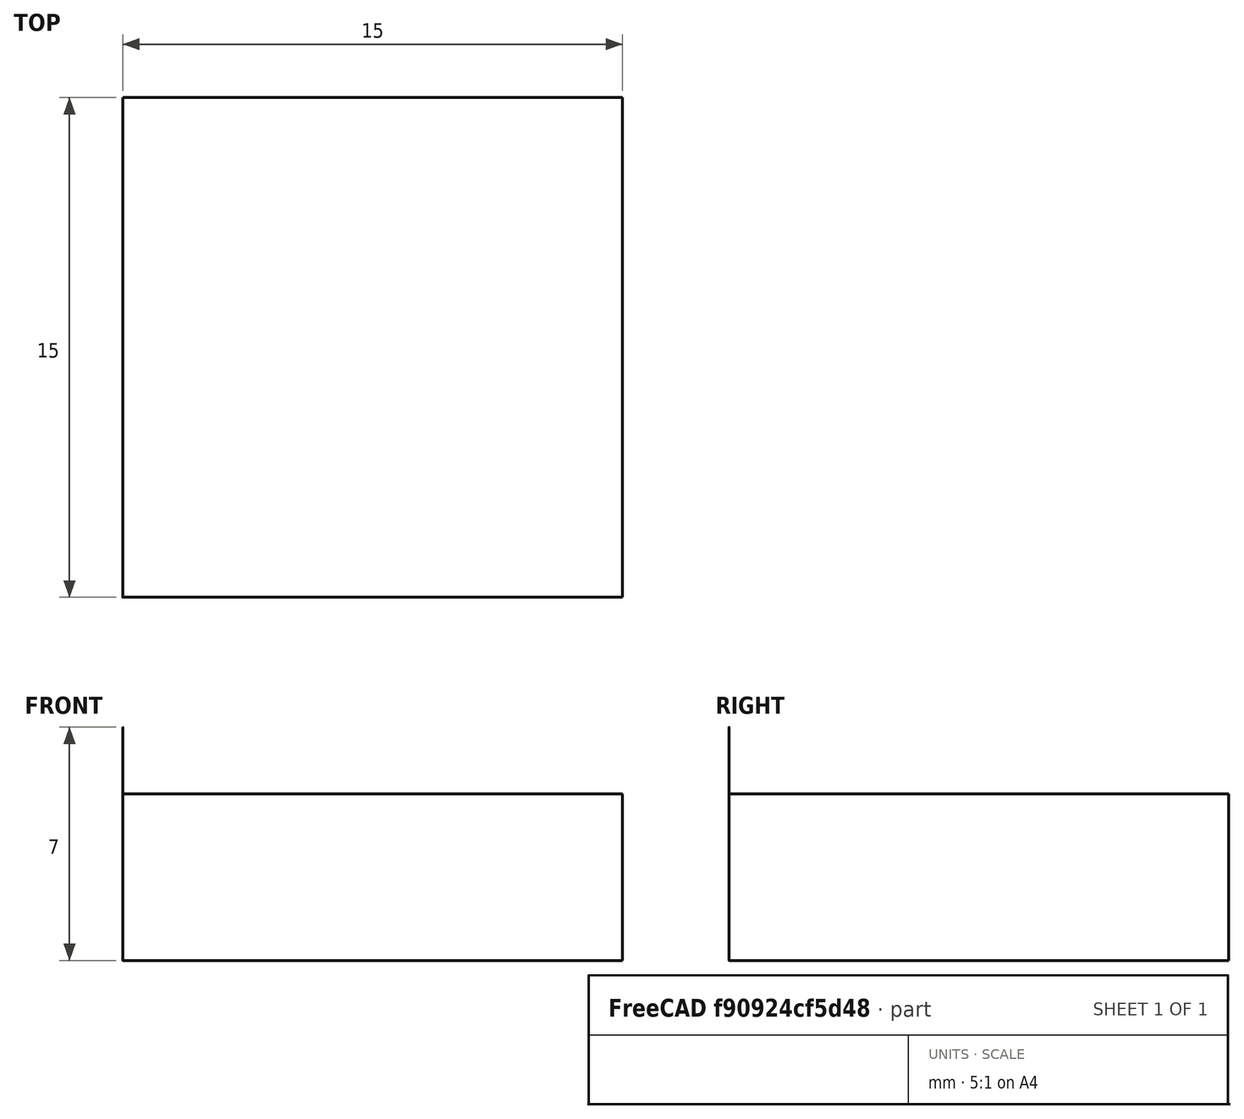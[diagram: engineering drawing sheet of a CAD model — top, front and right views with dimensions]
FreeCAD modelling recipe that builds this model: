
FCSTD DOCUMENT  (FreeCAD 1.0R39109 (Git))
Label: BoxWith25GridPockets
License: All rights reserved
LicenseURL: https://en.wikipedia.org/wiki/All_rights_reserved
objects: Part::Box×26, Part::Cut×25, Part::FeaturePython×4, App::DocumentObjectGroup×3, Path::FeaturePython×3, App::FeaturePython×1
note: 56 computed .brp shape members not serialized (recipe doc carries the construction recipe); baked Part::Feature solids carry a one-line shape summary decoded from their .brp

FEATURE [Part::Box] Box
  AttacherType = Attacher::AttachEngine3D
  Height = 5
  Length = 15
  Width = 15
FEATURE [Part::Box] Pocket_0_0
  AttacherType = Attacher::AttachEngine3D
  Height = 0.05
  Length = 0.2
  Placement = pos=(2.33333,2.33333,4.95) rot=(0,0,1;0rad)
  Width = 0.2
FEATURE [Part::Box] Pocket_0_1
  AttacherType = Attacher::AttachEngine3D
  Height = 0.05
  Length = 0.2
  Placement = pos=(4.86667,2.33333,4.95) rot=(0,0,1;0rad)
  Width = 0.2
FEATURE [Part::Box] Pocket_0_2
  AttacherType = Attacher::AttachEngine3D
  Height = 0.05
  Length = 0.2
  Placement = pos=(7.4,2.33333,4.95) rot=(0,0,1;0rad)
  Width = 0.2
FEATURE [Part::Box] Pocket_0_3
  AttacherType = Attacher::AttachEngine3D
  Height = 0.05
  Length = 0.2
  Placement = pos=(9.93333,2.33333,4.95) rot=(0,0,1;0rad)
  Width = 0.2
FEATURE [Part::Box] Pocket_0_4
  AttacherType = Attacher::AttachEngine3D
  Height = 0.05
  Length = 0.2
  Placement = pos=(12.4667,2.33333,4.95) rot=(0,0,1;0rad)
  Width = 0.2
FEATURE [Part::Box] Pocket_1_0
  AttacherType = Attacher::AttachEngine3D
  Height = 0.05
  Length = 0.2
  Placement = pos=(2.33333,4.86667,4.95) rot=(0,0,1;0rad)
  Width = 0.2
FEATURE [Part::Box] Pocket_1_1
  AttacherType = Attacher::AttachEngine3D
  Height = 0.05
  Length = 0.2
  Placement = pos=(4.86667,4.86667,4.95) rot=(0,0,1;0rad)
  Width = 0.2
FEATURE [Part::Box] Pocket_1_2
  AttacherType = Attacher::AttachEngine3D
  Height = 0.05
  Length = 0.2
  Placement = pos=(7.4,4.86667,4.95) rot=(0,0,1;0rad)
  Width = 0.2
FEATURE [Part::Box] Pocket_1_3
  AttacherType = Attacher::AttachEngine3D
  Height = 0.05
  Length = 0.2
  Placement = pos=(9.93333,4.86667,4.95) rot=(0,0,1;0rad)
  Width = 0.2
FEATURE [Part::Box] Pocket_1_4
  AttacherType = Attacher::AttachEngine3D
  Height = 0.05
  Length = 0.2
  Placement = pos=(12.4667,4.86667,4.95) rot=(0,0,1;0rad)
  Width = 0.2
FEATURE [Part::Box] Pocket_2_0
  AttacherType = Attacher::AttachEngine3D
  Height = 0.05
  Length = 0.2
  Placement = pos=(2.33333,7.4,4.95) rot=(0,0,1;0rad)
  Width = 0.2
FEATURE [Part::Box] Pocket_2_1
  AttacherType = Attacher::AttachEngine3D
  Height = 0.05
  Length = 0.2
  Placement = pos=(4.86667,7.4,4.95) rot=(0,0,1;0rad)
  Width = 0.2
FEATURE [Part::Box] Pocket_2_2
  AttacherType = Attacher::AttachEngine3D
  Height = 0.05
  Length = 0.2
  Placement = pos=(7.4,7.4,4.95) rot=(0,0,1;0rad)
  Width = 0.2
FEATURE [Part::Box] Pocket_2_3
  AttacherType = Attacher::AttachEngine3D
  Height = 0.05
  Length = 0.2
  Placement = pos=(9.93333,7.4,4.95) rot=(0,0,1;0rad)
  Width = 0.2
FEATURE [Part::Box] Pocket_2_4
  AttacherType = Attacher::AttachEngine3D
  Height = 0.05
  Length = 0.2
  Placement = pos=(12.4667,7.4,4.95) rot=(0,0,1;0rad)
  Width = 0.2
FEATURE [Part::Box] Pocket_3_0
  AttacherType = Attacher::AttachEngine3D
  Height = 0.05
  Length = 0.2
  Placement = pos=(2.33333,9.93333,4.95) rot=(0,0,1;0rad)
  Width = 0.2
FEATURE [Part::Box] Pocket_3_1
  AttacherType = Attacher::AttachEngine3D
  Height = 0.05
  Length = 0.2
  Placement = pos=(4.86667,9.93333,4.95) rot=(0,0,1;0rad)
  Width = 0.2
FEATURE [Part::Box] Pocket_3_2
  AttacherType = Attacher::AttachEngine3D
  Height = 0.05
  Length = 0.2
  Placement = pos=(7.4,9.93333,4.95) rot=(0,0,1;0rad)
  Width = 0.2
FEATURE [Part::Box] Pocket_3_3
  AttacherType = Attacher::AttachEngine3D
  Height = 0.05
  Length = 0.2
  Placement = pos=(9.93333,9.93333,4.95) rot=(0,0,1;0rad)
  Width = 0.2
FEATURE [Part::Box] Pocket_3_4
  AttacherType = Attacher::AttachEngine3D
  Height = 0.05
  Length = 0.2
  Placement = pos=(12.4667,9.93333,4.95) rot=(0,0,1;0rad)
  Width = 0.2
FEATURE [Part::Box] Pocket_4_0
  AttacherType = Attacher::AttachEngine3D
  Height = 0.05
  Length = 0.2
  Placement = pos=(2.33333,12.4667,4.95) rot=(0,0,1;0rad)
  Width = 0.2
FEATURE [Part::Box] Pocket_4_1
  AttacherType = Attacher::AttachEngine3D
  Height = 0.05
  Length = 0.2
  Placement = pos=(4.86667,12.4667,4.95) rot=(0,0,1;0rad)
  Width = 0.2
FEATURE [Part::Box] Pocket_4_2
  AttacherType = Attacher::AttachEngine3D
  Height = 0.05
  Length = 0.2
  Placement = pos=(7.4,12.4667,4.95) rot=(0,0,1;0rad)
  Width = 0.2
FEATURE [Part::Box] Pocket_4_3
  AttacherType = Attacher::AttachEngine3D
  Height = 0.05
  Length = 0.2
  Placement = pos=(9.93333,12.4667,4.95) rot=(0,0,1;0rad)
  Width = 0.2
FEATURE [Part::Box] Pocket_4_4
  AttacherType = Attacher::AttachEngine3D
  Height = 0.05
  Length = 0.2
  Placement = pos=(12.4667,12.4667,4.95) rot=(0,0,1;0rad)
  Width = 0.2
FEATURE [Part::Cut] Cut  label="Cut_0"
  Base = -> Box
  Refine = true
  Tool = -> Pocket_0_0
FEATURE [Part::Cut] Cut001  label="Cut_1"
  Base = -> Cut
  Refine = true
  Tool = -> Pocket_0_1
FEATURE [Part::Cut] Cut002  label="Cut_2"
  Base = -> Cut001
  Refine = true
  Tool = -> Pocket_0_2
FEATURE [Part::Cut] Cut003  label="Cut_3"
  Base = -> Cut002
  Refine = true
  Tool = -> Pocket_0_3
FEATURE [Part::Cut] Cut004  label="Cut_4"
  Base = -> Cut003
  Refine = true
  Tool = -> Pocket_0_4
FEATURE [Part::Cut] Cut005  label="Cut_5"
  Base = -> Cut004
  Refine = true
  Tool = -> Pocket_1_0
FEATURE [Part::Cut] Cut006  label="Cut_6"
  Base = -> Cut005
  Refine = true
  Tool = -> Pocket_1_1
FEATURE [Part::Cut] Cut007  label="Cut_7"
  Base = -> Cut006
  Refine = true
  Tool = -> Pocket_1_2
FEATURE [Part::Cut] Cut008  label="Cut_8"
  Base = -> Cut007
  Refine = true
  Tool = -> Pocket_1_3
FEATURE [Part::Cut] Cut009  label="Cut_9"
  Base = -> Cut008
  Refine = true
  Tool = -> Pocket_1_4
FEATURE [Part::Cut] Cut010  label="Cut_10"
  Base = -> Cut009
  Refine = true
  Tool = -> Pocket_2_0
FEATURE [Part::Cut] Cut011  label="Cut_11"
  Base = -> Cut010
  Refine = true
  Tool = -> Pocket_2_1
FEATURE [Part::Cut] Cut012  label="Cut_12"
  Base = -> Cut011
  Refine = true
  Tool = -> Pocket_2_2
FEATURE [Part::Cut] Cut013  label="Cut_13"
  Base = -> Cut012
  Refine = true
  Tool = -> Pocket_2_3
FEATURE [Part::Cut] Cut014  label="Cut_14"
  Base = -> Cut013
  Refine = true
  Tool = -> Pocket_2_4
FEATURE [Part::Cut] Cut015  label="Cut_15"
  Base = -> Cut014
  Refine = true
  Tool = -> Pocket_3_0
FEATURE [Part::Cut] Cut016  label="Cut_16"
  Base = -> Cut015
  Refine = true
  Tool = -> Pocket_3_1
FEATURE [Part::Cut] Cut017  label="Cut_17"
  Base = -> Cut016
  Refine = true
  Tool = -> Pocket_3_2
FEATURE [Part::Cut] Cut018  label="Cut_18"
  Base = -> Cut017
  Refine = true
  Tool = -> Pocket_3_3
FEATURE [Part::Cut] Cut019  label="Cut_19"
  Base = -> Cut018
  Refine = true
  Tool = -> Pocket_3_4
FEATURE [Part::Cut] Cut020  label="Cut_20"
  Base = -> Cut019
  Refine = true
  Tool = -> Pocket_4_0
FEATURE [Part::Cut] Cut021  label="Cut_21"
  Base = -> Cut020
  Refine = true
  Tool = -> Pocket_4_1
FEATURE [Part::Cut] Cut022  label="Cut_22"
  Base = -> Cut021
  Refine = true
  Tool = -> Pocket_4_2
FEATURE [Part::Cut] Cut023  label="Cut_23"
  Base = -> Cut022
  Refine = true
  Tool = -> Pocket_4_3
FEATURE [Part::Cut] Cut024  label="Cut_24"
  Base = -> Cut023
  Refine = true
  Tool = -> Pocket_4_4
FEATURE [App::FeaturePython] SetupSheet  # Path/CAM operation (typed FeaturePython)
  ClearanceHeightExpression = OpStockZMax+SetupSheet.ClearanceHeightOffset
  ClearanceHeightOffset = 5
  CoolantMode = 0
  CoolantModes = None | Flood | Mist
  FinalDepthExpression = OpFinalDepth
  HorizRapid = 333.333
  SafeHeightExpression = OpStockZMax+SetupSheet.SafeHeightOffset
  SafeHeightOffset = 3
  StartDepthExpression = OpStartDepth
  StepDownExpression = OpToolDiameter
  VertRapid = 0
FEATURE [Part::FeaturePython] Clone  label="Model-Cut_24"  # Draft clone (typed FeaturePython)
  AttacherType = Attacher::AttachEngine3D
  Fuse = false
  Objects = -> [Cut024]
  PathResource = Model
  Scale = (1,1,1)
FEATURE [App::DocumentObjectGroup] Model
  Group = -> [Clone]
FEATURE [Part::FeaturePython] ToolBit  label="Drill"  # Path/CAM toolbit (typed FeaturePython)
  BitPropertyNames = Chipload | Diameter | Flutes | Length | Material | TipAngle
  BitShape = <path>
  Chipload = 0
  Diameter = 0.005
  Flutes = 0
  Length = 7
  Material = 0
  ShapeName = drill
  TipAngle = 119
FEATURE [Part::FeaturePython] Stock  # WARN: FeaturePython — macro-defined, semantics opaque (R4)
  Base = -> Model
  ExtXneg = 0.001
  ExtXpos = 0.001
  ExtYneg = 0.001
  ExtYpos = 0.001
  ExtZneg = 0.001
  ExtZpos = 0.001
  StockType = FromBase
FEATURE [Part::FeaturePython] ToolBit001  label="Drill003"  # Path/CAM toolbit (typed FeaturePython)
  BitPropertyNames = Chipload | Diameter | Flutes | Length | Material | TipAngle
  BitShape = <path>
  Chipload = 0
  Diameter = 0.005
  Flutes = 0
  Length = 7
  Material = 0
  ShapeName = drill
  TipAngle = 119
FEATURE [Path::FeaturePython] TC__Default_Tool  label="TC: Default Tool"  # Path/CAM operation (typed FeaturePython)
  HorizFeed = 0
  HorizRapid = 333.333
  SpindleDir = 0
  SpindleSpeed = 0
  Tool = -> ToolBit001
  ToolNumber = 1
  VertFeed = 0
  VertRapid = 0
  expr: HorizRapid = SetupSheet.HorizRapid
  expr: VertRapid = SetupSheet.VertRapid
FEATURE [App::DocumentObjectGroup] Tools
  Group = -> [TC__Default_Tool]
FEATURE [Path::FeaturePython] Pocket_Shape  # Path/CAM operation (typed FeaturePython)
  Active = true
  AreaParams:
    Tolerance = 1e-07
    FitArcs = True
    Simplify = False
    CleanDistance = 0.0
    Accuracy = 0.01
    Unit = 1.0
    MinArcPoints = 4
    MaxArcPoints = 100
    ClipperScale = 10000000.0
    Fill = 0
    Coplanar = 0
    Reorient = True
    Outline = False
    Explode = False
    OpenMode = 0
    Deflection = 0.01
    SubjectFill = 0
    ClipFill = 0
    Offset = 0.0
    ExtraPass = 0
    Stepover = 0.0
    LastStepover = 0.0
    JoinType = 0
    EndType = 0
    MiterLimit = 2.0
    RoundPrecision = 0.0
    PocketMode = 1
    ToolRadius = 0.0025
    PocketExtraOffset = 0.0
    PocketStepover = 0.0025
    PocketLastStepover = 0.0
    FromCenter = True
    Angle = 0.0
    AngleShift = 0.0
    Shift = 0.0
    Thicken = False
    SectionCount = -1
    Stepdown = 1.0
    SectionOffset = 0.0
    SectionTolerance = 1e-06
    SectionMode = 2
    Project = False
  Base = -> [Clone]
  ClearanceHeight = 10.001
  CoolantMode = 0
  CutMode = 0
  CycleTime = Cycletime Error
  ExtensionCorners = true
  ExtensionLengthDefault = 0.0025
  ExtraOffset = 0
  FinalDepth = 4.95
  FinishDepth = 0
  KeepToolDown = false
  MinTravel = false
  OffsetPattern = 0
  OpFinalDepth = 4.95
  OpStartDepth = 5.001
  OpStockZMax = 5.001
  OpStockZMin = -0.001
  OpToolDiameter = 0.005
  PathParams = {'orientation': 1, 'feedrate': 0.0, 'feedrate_v': 0.0, 'verbose': True, 'resume_height': 8.001000000000001, 'retraction': 10.001000000000001, 'return_end': True, 'preamble': False, 'start': Vector (12.664166566666669, 10.130833333333333, 10.001000000000001)}
  PocketLastStepOver = 0
  SafeHeight = 8.001
  SplitArcs = false
  StartAt = 0
  StartDepth = 5.001
  StartPoint = (0,0,0)
  StepDown = 0.005
  StepOver = 50
  ToolController = -> TC__Default_Tool
  UseOutline = false
  UseRestMachining = false
  UseStartPoint = false
  ZigZagAngle = 0
  expr: ClearanceHeight = OpStockZMax + SetupSheet.ClearanceHeightOffset
  expr: ExtensionLengthDefault = OpToolDiameter / 2
  expr: FinalDepth = OpFinalDepth
  expr: SafeHeight = OpStockZMax + SetupSheet.SafeHeightOffset
  expr: StartDepth = OpStartDepth
  expr: StepDown = OpToolDiameter
FEATURE [App::DocumentObjectGroup] Operations
  Group = -> [Pocket_Shape]
FEATURE [Path::FeaturePython] Job  # Path/CAM operation (typed FeaturePython)
  CycleTime = 00:00:00
  Fixtures = G54
  GeometryTolerance = 0.01
  JobType = 0
  Model = -> Model
  Operations = -> Operations
  OrderOutputBy = 0
  PostProcessor = 14
  PostProcessorOutputFile = <userpath>/Desktop/freecad/laser25pockets.gcode
  SetupSheet = -> SetupSheet
  SplitOutput = false
  Stock = -> Stock
  Tools = -> Tools
note: 2 file-system paths scrubbed to <path> (originals preserved in the JSON sidecar)
